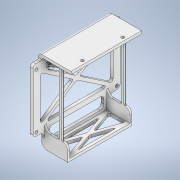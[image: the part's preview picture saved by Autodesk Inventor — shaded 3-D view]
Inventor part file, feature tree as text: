
AUTODESK INVENTOR PART (.ipt)
format: ipt  version: 2022 (Build 260153000, 153)  size: 804,352 bytes
history: native  units: in
note: dims shown in document units (in); Inventor stores cm internally (conversion verified against a paired STEP export)
features: fillet x18, sketch x17, extrude x15, mirror x3, hole x2, plane x1
ambient origin geometry x8: Origin, YZ Plane, XZ Plane, XY Plane, X Axis, Y Axis, Z Axis, Center Point
bodies: Solid1 (feature_tree)
feature tree (56):
  extrude  "Extrusion1"  Depth=1.3701in
  extrude  "Extrusion2"  Depth=1.252in
  plane  "Work Plane1"
  extrude  "Extrusion4"  Depth=0.1181in
  fillet  "Fillet1"  Radius=0.1181in
  mirror  "Mirror2"
  hole  "Hole2"  [1 undecoded]
  extrude  "Extrusion19"  Depth=0.1181in TaperAngle=0.0deg
  fillet  "Fillet14"  Radius=0.0394in
  extrude  "Extrusion20"  Depth=0.6339in
  fillet  "Fillet16"  Radius=0.1496in
  fillet  "Fillet17"  Radius=0.6339in
  hole  "Hole4"  [1 undecoded]
  extrude  "Extrusion24"  Depth=0.3937in
  fillet  "Fillet21"  Radius=0.3484in
  fillet  "Fillet22"  Radius=0.3937in
  fillet  "Fillet23"  Radius=3.0748in
  extrude  "Extrusion25"  Depth=0.2953in
  fillet  "Fillet24"  Radius=0.2992in
  extrude  "Extrusion26"  Depth=0.3937in
  mirror  "Mirror7"
  fillet  "Fillet25"  Radius=0.0557in
  fillet  "Fillet27"  Radius=0.1378in
  fillet  "Fillet28"  Radius=0.1378in
  extrude  "Extrusion27"  Depth=2.2913in
  extrude  "Extrusion28"  Depth=0.1378in
  extrude  "Extrusion29"  Depth=0.1378in
  extrude  "Extrusion30"  Depth=0.3937in TaperAngle=0.0deg
  extrude  "Extrusion31"  Depth=0.1575in
  fillet  "Fillet30"  Radius=0.0591in
  fillet  "Fillet31"  Radius=0.1575in
  fillet  "Fillet32"  Radius=2.4567in
  fillet  "Fillet35"  Radius=0.1496in
  extrude  "Extrusion33"  Depth=0.1575in TaperAngle=0.0deg
  fillet  "Fillet36"  Radius=0.1148in
  mirror  "Mirror9"
  fillet  "Fillet37"  Radius=0.1575in
  extrude  "Extrusion34"  Depth=0.1575in
  fillet  "Fillet38"  Radius=0.0394in
  sketch  "Sketch1"  dims[d0=1.3701in d1=2.9685in]
  sketch  "Sketch2"  dims[d2=1.6024in d3=0.0in d4=1.252in]
  sketch  "Sketch4"  dims[d5=1.4843in d6=0.0in d17=0.1181in d18=0.1181in]
  sketch  "Sketch22"  dims[d19=0.1457in d20=0.1575in]
  sketch  "Sketch24"  dims[d21=0.1102in d22=0.1181in d23=0.0in d24=0.0394in]
  sketch  "Sketch26"  dims[d80=0.2697in d126=0.6339in d127=0.1496in d128=0.6339in]
  sketch  "Sketch30"  dims[d129=0.124in d130=0.2362in d131=0.1575in d132=0.0787in d133=90.0deg d134=0.315in d135=0.8108in d170=3.6654in]
  sketch  "Sketch31"  dims[d171=2.649in d172=1.3695in d173=0.3484in d174=0.3937in d175=0.0in d192=3.0748in]
  sketch  "Sketch32"  dims[d193=1.9685in d194=0.2953in d195=0.2992in]
  sketch  "Sketch33"  dims[d196=0.3937in d197=0.0in d204=0.124in d205=0.124in d208=0.0557in d222=0.1378in d223=0.1378in]
  sketch  "Sketch34"  dims[d224=3.3898in d225=2.2913in]
  sketch  "Sketch35"  dims[d226=2.2913in d227=0.1378in]
  sketch  "Sketch36"  dims[d228=3.3898in d229=0.1378in]
  sketch  "Sketch37"  dims[d230=0.1299in d231=0.2362in d232=0.1575in d233=0.0787in d234=90.0deg d235=0.315in d236=0.8108in d238=0.3937in d239=0.0in]
  sketch  "Sketch38"  dims[d240=0.1575in d241=0.0787in d242=0.0591in d243=0.1575in d244=2.4567in d245=0.1496in]
  sketch  "Sketch40"  dims[d246=0.2559in d247=0.0787in d248=0.0in d249=0.1148in d250=0.1575in d251=0.0in]
  sketch  "Sketch41"  dims[d252=0.1181in d254=0.0394in d255=0.0394in d256=0.1181in d257=2.6969in d258=0.6457in d259=0.0in d260=0.1181in d261=0.9843in d262=0.0in d263=0.0787in d264=0.5276in d265=0.0787in d266=0.5276in d267=0.9843in d268=0.0in d270=0.7514in d271=2.4606in d272=0.1181in d273=0.9843in d274=0.0in d275=0.1181in d276=0.1181in d277=0.1181in d278=0.0591in d279=0.0591in d280=2.5787in d281=0.7514in d282=2.4606in d283=0.7514in d284=0.0591in d285=0.1738in d286=0.3937in d287=0.0in d288=0.0315in d289=0.0591in d290=0.1969in d296=0.3602in d298=0.2362in d299=0.1575in d300=0.0787in d301=0.9843in d302=0.0in d303=0.0354in d304=0.0354in d305=2.3031in d306=0.4941in d307=0.1181in d308=0.1181in d309=0.3937in d310=0.0in d311=0.1575in d105=0.0in d106=0.0in d107=0.0in d108=0.0in d119=0.0197in d120=0.0344in d121=0.0197in d122=0.0344in d143=0.0394in d144=0.0394in d145=0.0394in d146=0.0059in d147=0.1516in d148=0.0148in d149=0.5635in d150=0.0295in d151=0.8108in d152=0.0025in d153=0.0295in d154=0.0148in d166=0.0197in d167=0.0344in d168=0.0197in d169=0.0344in d209=0.0in d210=0.0in d211=0.0in d213=0.0197in d214=0.0344in d215=0.0197in d216=0.0344in]
note: 2 required parameter values undecoded (feature->parameter linkage not recoverable at this tier; creation-order binding heuristic only, values carry confidence <= 0.55)
